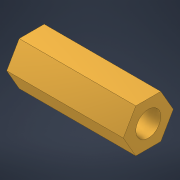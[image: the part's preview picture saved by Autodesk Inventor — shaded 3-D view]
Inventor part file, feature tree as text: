
AUTODESK INVENTOR PART (.ipt)
format: ipt  version: 2022 (Build 260153000, 153)  size: 97,280 bytes
history: native  units: mm
features: extrude x1, sketch x1
ambient origin geometry x8: Origin, YZ Plane, XZ Plane, XY Plane, X Axis, Y Axis, Z Axis, Center Point
bodies: Solid1 (feature_tree)
feature tree (2):
  extrude  "Extrusion1"  Depth=3.0mm
  sketch  "Sketch1"  dims[d0=6.0mm d1=3.0mm d2=14.0mm d3=0.0mm d4=5.196152mm]
